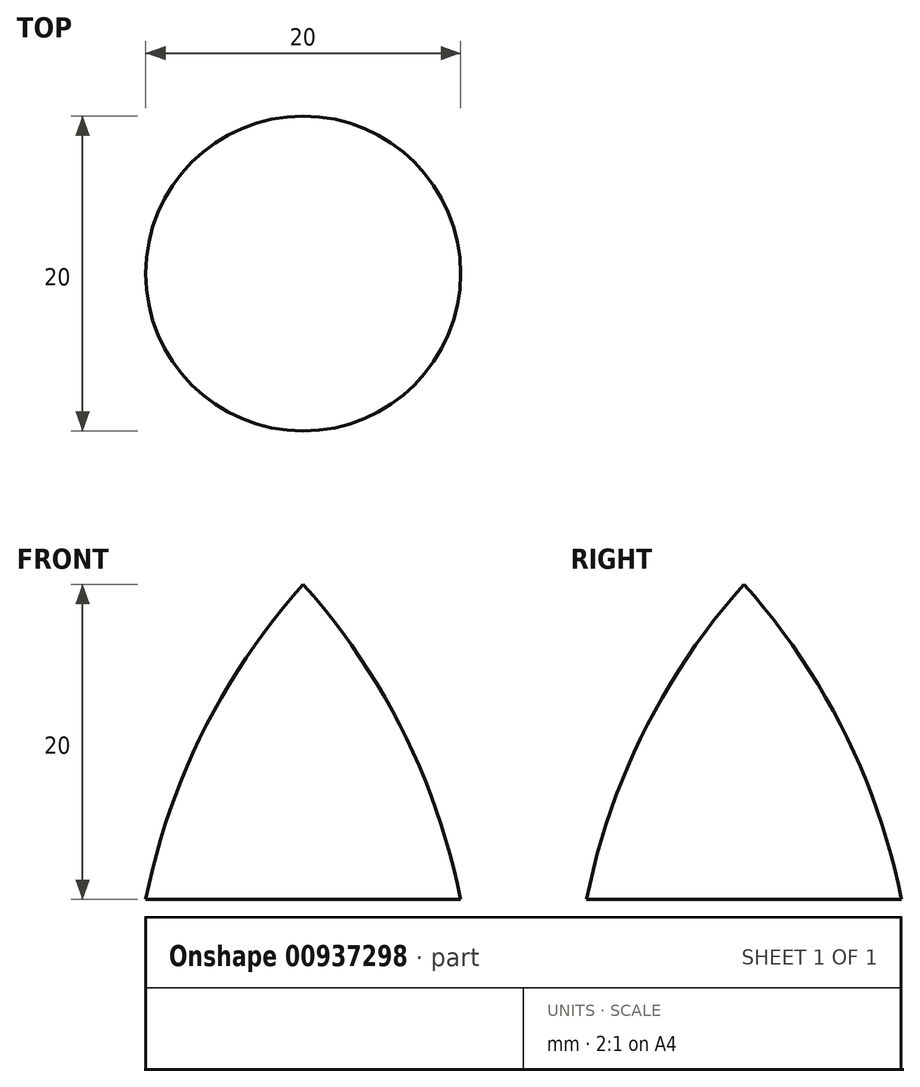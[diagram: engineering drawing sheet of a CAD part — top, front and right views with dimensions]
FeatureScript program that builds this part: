
annotation { "Feature Type Name" : "Feature", "Feature Type Description" : "" }
export const myFeature = defineFeature(function(context is Context, id is Id, definition is map)
    precondition{}
    {
        {
            var Q0;
            Q0=qCreatedBy(makeId("Front.planeOp"),FACE);
            var sketch = newSketch(context, id + "F0", { "sketchPlane" : qUnion([Q0])});
            skLineSegment(sketch, "E0", {"start": v(-0.5, 0) * mm, "end": v(-10, 0) * mm});
            skArc(sketch, "E1", {"start": v(0, 20) * mm, "mid": v(-6.35, 10.67) * mm, "end": v(-10, 0) * mm});
            skLineSegment(sketch, "E2", {"start": v(-0.5, 0) * mm, "end": v(-0.5, 3) * mm});
            skLineSegment(sketch, "E3", {"start": v(-0.5, 3) * mm, "end": v(0, 3) * mm});
            skLineSegment(sketch, "E4", {"start": v(0, 3) * mm, "end": v(0, 20) * mm});
            skSolve(sketch);
        }
        {
            var Q0;
            Q0=makeQuery(id+"F0.imprint","IMPRINT",FACE,{"disambiguationData":[TD([[makeQuery(id+"F0.imprint","IMPRINT",EDGE,{"derivedFrom":sQuery(id+"F0.wireOp",EDGE,"E0")}),-1.0]])]});
            var Q1;
            Q1=sQuery(id+"F0.wireOp",EDGE,"E1");
            var Q2;
            Q2=sQuery(id+"F0.wireOp",EDGE,"E4");
            revolve(context, id + "F1", {"bodyType" : ToolBodyType.SURFACE, "surfaceOperationType" : NewSurfaceOperationType.NEW, "entities" : qUnion([Q0]), "surfaceEntities" : qUnion([Q1]), "axis" : qUnion([Q2]), "revolveType" : RevolveType.FULL});
        }
    });
